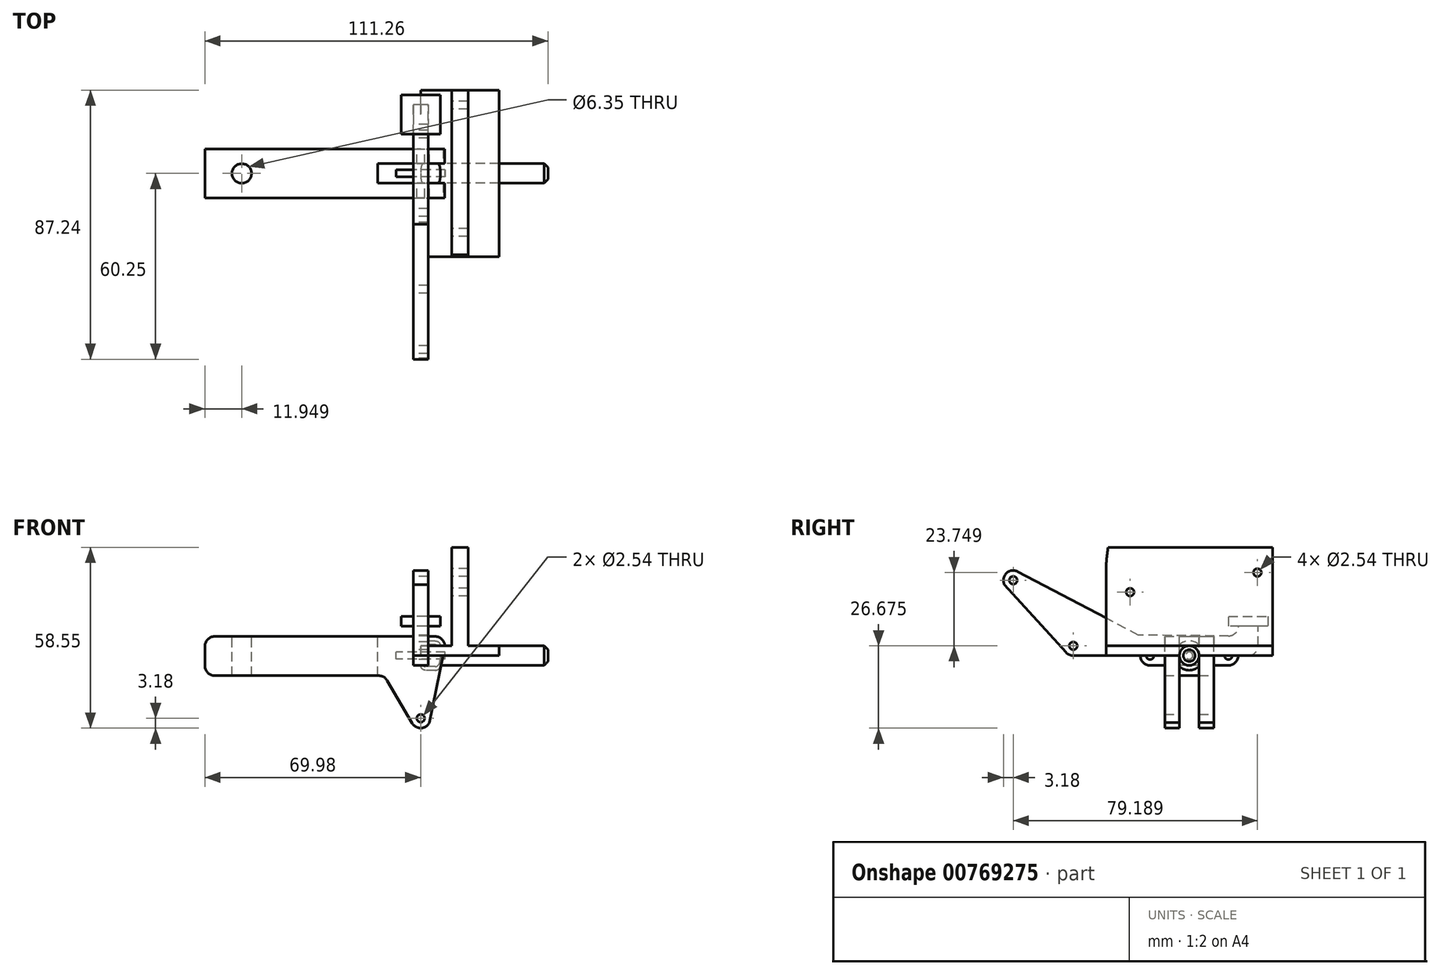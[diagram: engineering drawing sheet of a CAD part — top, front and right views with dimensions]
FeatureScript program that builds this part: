
annotation { "Feature Type Name" : "Feature", "Feature Type Description" : "" }
export const myFeature = defineFeature(function(context is Context, id is Id, definition is map)
    precondition{}
    {
        {
            var Q0;
            Q0=qCreatedBy(makeId("Front.planeOp"),FACE);
            var sketch = newSketch(context, id + "F0", { "sketchPlane" : qUnion([Q0])});
            skCircle(sketch, "E0", {"center": v(0, 0) * mm, "radius": 1.27 * mm});
            skLineSegment(sketch, "E1", {"start": v(-24.73, 6.19) * mm, "end": v(4.64, 6.19) * mm});
            skLineSegment(sketch, "E2", {"start": v(7.75, 2.38) * mm, "end": v(2.83, -21.75) * mm});
            skLineSegment(sketch, "E3", {"start": v(-2.74, -21.93) * mm, "end": v(-10.89, -8.08) * mm});
            skLineSegment(sketch, "E4", {"start": v(-13.62, -6.51) * mm, "end": v(-66.8, -6.51) * mm});
            skLineSegment(sketch, "E5", {"start": v(-69.98, -3.34) * mm, "end": v(-69.98, 3.01) * mm});
            skLineSegment(sketch, "E6", {"start": v(-66.8, 6.19) * mm, "end": v(-24.73, 6.19) * mm});
            skPoint(sketch, "E7.visualSharp", {"position": v(8.53, 6.19) * mm});
            skArc(sketch, "E7.filletArc", {"start": v(7.75, 2.38) * mm, "mid": v(7.1, 5.02) * mm, "end": v(4.64, 6.19) * mm});
            skPoint(sketch, "E8.visualSharp", {"position": v(-11.8, -6.51) * mm});
            skArc(sketch, "E8.filletArc", {"start": v(-10.89, -8.08) * mm, "mid": v(-12.05, -6.93) * mm, "end": v(-13.62, -6.51) * mm});
            skPoint(sketch, "E9.visualSharp", {"position": v(-69.98, 6.19) * mm});
            skArc(sketch, "E9.filletArc", {"start": v(-66.8, 6.19) * mm, "mid": v(-69.05, 5.26) * mm, "end": v(-69.98, 3.01) * mm});
            skPoint(sketch, "E10.visualSharp", {"position": v(-69.98, -6.51) * mm});
            skArc(sketch, "E10.filletArc", {"start": v(-69.98, -3.34) * mm, "mid": v(-69.05, -5.58) * mm, "end": v(-66.8, -6.51) * mm});
            skArc(sketch, "E11", {"start": v(-2.74, -21.93) * mm, "mid": v(0.1, -23.5) * mm, "end": v(2.83, -21.75) * mm});
            skLineSegment(sketch, "E12", {"start": v(0, 0) * mm, "end": v(-69.98, -0.16) * mm, "construction": true});
            skCircle(sketch, "E13", {"center": v(0, -20.32) * mm, "radius": 1.27 * mm});
            skLineSegment(sketch, "E14", {"start": v(0, 0) * mm, "end": v(0, -20.32) * mm, "construction": true});
            skSolve(sketch);
        }
        {
            var Q0;
            Q0=qSketchRegion(id+"F0",true);
            extrude(context, id + "F1", {"entities" : qUnion([Q0]), "endBound" : BoundingType.SYMMETRIC, "depth" : 15.88 * mm, "offsetDistance" : 25.4 * mm});
        }
        {
            var Q0;
            Q0=makeQuery(id+"F1.opExtrude","SWEPT_FACE",FACE,{"disambiguationData":[OSD([sQuery(id+"F0.wireOp",EDGE,"E1"),sQuery(id+"F0.wireOp",EDGE,"E6")])]});
            var sketch = newSketch(context, id + "F2", { "sketchPlane" : qUnion([Q0])});
            skLineSegment(sketch, "E15.0", {"start": v(7.75, -7.94) * mm, "end": v(7.75, 7.94) * mm});
            skLineSegment(sketch, "E16", {"start": v(7.75, 3.18) * mm, "end": v(-13.88, 3.18) * mm});
            skLineSegment(sketch, "E17", {"start": v(-13.88, 3.18) * mm, "end": v(-13.88, -3.17) * mm});
            skLineSegment(sketch, "E18", {"start": v(-13.88, -3.17) * mm, "end": v(7.75, -3.17) * mm});
            skLineSegment(sketch, "E19", {"start": v(7.75, 0) * mm, "end": v(-66.8, 0) * mm, "construction": true});
            skCircle(sketch, "E20", {"center": v(-58.03, 0) * mm, "radius": 3.18 * mm});
            skLineSegment(sketch, "E21.0", {"start": v(-66.8, 7.94) * mm, "end": v(4.64, 7.94) * mm});
            skLineSegment(sketch, "E22.0", {"start": v(-66.8, -7.94) * mm, "end": v(4.64, -7.94) * mm});
            skSolve(sketch);
        }
        {
            var Q0;
            Q0=qSketchRegion(id+"F2",true);
            extrude(context, id + "F3", {"entities" : qUnion([Q0]), "operationType" : NewBodyOperationType.REMOVE, "endBound" : BoundingType.THROUGH_ALL, "oppositeDirection" : true, "depth" : 25.4 * mm, "offsetDistance" : 25.4 * mm});
        }
        {
            var Q0;
            {var subQ2=sQuery(id+"F0.wireOp",EDGE,"E2");Q0=makeQuery(id+"F3.boolean.opBoolean","SPLIT",FACE,{"disambiguationData":[TD([makeQuery(id+"F3.opExtrude","SWEPT_FACE",FACE,{"disambiguationData":[OSD([sQuery(id+"F2.wireOp",EDGE,"E16")])]})])],"derivedFrom":makeQuery(id+"F1.opExtrude","SWEPT_FACE",FACE,{"disambiguationData":[OSD([subQ2])]})});}
            var sketch = newSketch(context, id + "F4", { "sketchPlane" : qUnion([Q0])});
            skLineSegment(sketch, "E23.0", {"start": v(-3.17, 3.88) * mm, "end": v(3.18, 3.88) * mm});
            skLineSegment(sketch, "E24.0", {"start": v(3.18, 5.12) * mm, "end": v(-3.17, 5.12) * mm});
            skLineSegment(sketch, "E25", {"start": v(3.18, 5.12) * mm, "end": v(3.18, 3.88) * mm});
            skLineSegment(sketch, "E26", {"start": v(-3.17, 5.12) * mm, "end": v(-3.17, 3.88) * mm});
            skSolve(sketch);
        }
        {
            var Q0;
            Q0=qSketchRegion(id+"F4",true);
            extrude(context, id + "F5", {"entities" : qUnion([Q0]), "operationType" : NewBodyOperationType.REMOVE, "oppositeDirection" : true, "depth" : 7.85 * mm, "offsetDistance" : 25.4 * mm});
        }
        {
            var Q0;
            Q0=qCreatedBy(makeId("Front.planeOp"),FACE);
            var sketch = newSketch(context, id + "F6", { "sketchPlane" : qUnion([Q0])});
            skLineSegment(sketch, "E27", {"start": v(0, 0) * mm, "end": v(25.4, 0) * mm});
            skLineSegment(sketch, "E28", {"start": v(0, 0) * mm, "end": v(0, 3.18) * mm});
            skLineSegment(sketch, "E29", {"start": v(0, 3.18) * mm, "end": v(15.36, 3.18) * mm});
            skLineSegment(sketch, "E30", {"start": v(25.4, 0) * mm, "end": v(25.4, 3.18) * mm});
            skLineSegment(sketch, "E31", {"start": v(25.4, 3.18) * mm, "end": v(10.04, 3.18) * mm});
            skLineSegment(sketch, "E32", {"start": v(15.36, 3.18) * mm, "end": v(15.36, 35.05) * mm});
            skLineSegment(sketch, "E33", {"start": v(10.04, 35.05) * mm, "end": v(15.36, 35.05) * mm});
            skLineSegment(sketch, "E34", {"start": v(10.04, 35.05) * mm, "end": v(10.04, 3.18) * mm});
            skSolve(sketch);
        }
        {
            var Q0;
            Q0=qSketchRegion(id+"F6",true);
            extrude(context, id + "F7", {"entities" : qUnion([Q0]), "endBound" : BoundingType.SYMMETRIC, "depth" : 53.97 * mm, "offsetDistance" : 25.4 * mm});
        }
        {
            var Q0;
            Q0=makeQuery(id+"F7.opExtrude","SWEPT_FACE",FACE,{"disambiguationData":[OSD([sQuery(id+"F6.wireOp",EDGE,"E34")])]});
            var sketch = newSketch(context, id + "F8", { "sketchPlane" : qUnion([Q0])});
            skLineSegment(sketch, "E35.0.0", {"start": v(-26.99, 13.43) * mm, "end": v(-26.99, 3.18) * mm});
            skLineSegment(sketch, "E35.0.2", {"start": v(26.99, 3.18) * mm, "end": v(26.99, 26.92) * mm});
            skLineSegment(sketch, "E35.0.3", {"start": v(-26.99, 3.18) * mm, "end": v(26.99, 3.18) * mm});
            skPoint(sketch, "E36.visualSharp", {"position": v(26.99, 35.05) * mm});
            skLineSegment(sketch, "E37.0.0", {"start": v(-26.99, 0) * mm, "end": v(-26.99, 3.17) * mm});
            skLineSegment(sketch, "E37.0.1", {"start": v(-26.99, 3.17) * mm, "end": v(26.99, 3.17) * mm});
            skLineSegment(sketch, "E37.0.2", {"start": v(26.99, 3.17) * mm, "end": v(26.99, 0) * mm});
            skLineSegment(sketch, "E37.0.3", {"start": v(26.99, 0) * mm, "end": v(-26.99, 0) * mm});
            skArc(sketch, "E38", {"start": v(-71.23, 26.92) * mm, "mid": v(-22.12, 76.03) * mm, "end": v(26.99, 26.92) * mm});
            skCircle(sketch, "E39", {"center": v(-22.12, 26.92) * mm, "radius": 1.27 * mm});
            skLineSegment(sketch, "E40", {"start": v(-65.76, 17.46) * mm, "end": v(-71.23, 26.92) * mm});
            skLineSegment(sketch, "E41", {"start": v(-68.51, 12.7) * mm, "end": v(9.87, 12.7) * mm});
            skPoint(sketch, "E42.visualSharp", {"position": v(-63.01, 12.7) * mm});
            skArc(sketch, "E42.filletArc", {"start": v(-65.76, 17.46) * mm, "mid": v(-71.26, 17.46) * mm, "end": v(-68.51, 12.7) * mm});
            skPoint(sketch, "E43.visualSharp", {"position": v(12.82, 12.7) * mm});
            skArc(sketch, "E43.filletArc", {"start": v(9.87, 12.7) * mm, "mid": v(12.03, 13.55) * mm, "end": v(13.04, 15.65) * mm});
            skCircle(sketch, "E44", {"center": v(19.16, 20.57) * mm, "radius": 1.27 * mm});
            skLineSegment(sketch, "E45", {"start": v(13.04, 15.65) * mm, "end": v(15.32, 26.92) * mm});
            skLineSegment(sketch, "E46", {"start": v(15.32, 26.92) * mm, "end": v(22.7, 26.67) * mm});
            skLineSegment(sketch, "E47", {"start": v(22.7, 26.67) * mm, "end": v(-26.99, 13.43) * mm});
            skPoint(sketch, "E48.orphan", {"position": v(-26.99, 35.05) * mm});
            skSolve(sketch);
        }
        {
            var Q0;
            {var subQ4=sQuery(id+"F8.wireOp",EDGE,"E38");Q0=makeQuery(id+"F8.imprint","IMPRINT",FACE,{"disambiguationData":[TD([[makeQuery(id+"F8.imprint","IMPRINT",EDGE,{"derivedFrom":subQ4}),-1.0]])]});}
            var Q1;
            Q1=makeQuery(id+"F8.imprint","IMPRINT",FACE,{"disambiguationData":[TD([[makeQuery(id+"F8.imprint","IMPRINT",EDGE,{"derivedFrom":sQuery(id+"F8.wireOp",EDGE,"E39")}),1.0]])]});
            var Q2;
            Q2=makeQuery(id+"F8.imprint","IMPRINT",FACE,{"disambiguationData":[TD([[makeQuery(id+"F8.imprint","IMPRINT",EDGE,{"derivedFrom":sQuery(id+"F8.wireOp",EDGE,"E44")}),1.0]])]});
            extrude(context, id + "F9", {"entities" : qUnion([Q0, Q1, Q2]), "operationType" : NewBodyOperationType.REMOVE, "endBound" : BoundingType.THROUGH_ALL, "oppositeDirection" : true, "depth" : 25.4 * mm, "offsetDistance" : 25.4 * mm});
        }
        {
            var Q0;
            Q0=qCreatedBy(makeId("Right.planeOp"),FACE);
            var sketch = newSketch(context, id + "F10", { "sketchPlane" : qUnion([Q0])});
            skLineSegment(sketch, "E49", {"start": v(0, 0) * mm, "end": v(19.13, 0) * mm});
            skLineSegment(sketch, "E50", {"start": v(22.3, 3.18) * mm, "end": v(22.3, 6.35) * mm});
            skLineSegment(sketch, "E51", {"start": v(12.75, 6.38) * mm, "end": v(0, 6.49) * mm});
            skLineSegment(sketch, "E52", {"start": v(27.19, 9.52) * mm, "end": v(27.19, 0) * mm, "construction": true});
            skLineSegment(sketch, "E53", {"start": v(22.3, 3.17) * mm, "end": v(0, 3.17) * mm, "construction": true});
            skLineSegment(sketch, "E54", {"start": v(15.95, 9.55) * mm, "end": v(15.95, 9.55) * mm});
            skLineSegment(sketch, "E55", {"start": v(22.3, 6.35) * mm, "end": v(22.3, 9.55) * mm});
            skLineSegment(sketch, "E56", {"start": v(22.3, 9.55) * mm, "end": v(15.95, 9.55) * mm});
            skLineSegment(sketch, "E57", {"start": v(15.95, 9.55) * mm, "end": v(12.78, 9.55) * mm});
            skLineSegment(sketch, "E58", {"start": v(12.78, 9.55) * mm, "end": v(12.78, 12.73) * mm});
            skLineSegment(sketch, "E59", {"start": v(12.78, 12.73) * mm, "end": v(25.48, 12.73) * mm});
            skLineSegment(sketch, "E60", {"start": v(25.48, 12.73) * mm, "end": v(25.48, 9.55) * mm});
            skLineSegment(sketch, "E61", {"start": v(25.48, 9.55) * mm, "end": v(22.3, 9.55) * mm});
            skPoint(sketch, "E62.visualSharp", {"position": v(22.3, 0) * mm});
            skArc(sketch, "E62.filletArc", {"start": v(19.13, 0) * mm, "mid": v(21.37, 0.93) * mm, "end": v(22.3, 3.18) * mm});
            skPoint(sketch, "E63.visualSharp", {"position": v(15.95, 6.35) * mm});
            skArc(sketch, "E63.filletArc", {"start": v(12.75, 6.38) * mm, "mid": v(15.02, 7.3) * mm, "end": v(15.95, 9.55) * mm});
            skLineSegment(sketch, "E64", {"start": v(0, 6.49) * mm, "end": v(-16.47, 6.63) * mm});
            skLineSegment(sketch, "E65", {"start": v(-16.47, 6.63) * mm, "end": v(-55.6, 27.23) * mm});
            skLineSegment(sketch, "E66", {"start": v(0, 0) * mm, "end": v(-37.6, 0) * mm});
            skLineSegment(sketch, "E67", {"start": v(-39.95, 1.04) * mm, "end": v(-59.93, 23.04) * mm});
            skArc(sketch, "E68", {"start": v(-55.6, 27.23) * mm, "mid": v(-59.27, 26.7) * mm, "end": v(-59.93, 23.04) * mm});
            skPoint(sketch, "E69.visualSharp", {"position": v(-39, 0) * mm});
            skArc(sketch, "E69.filletArc", {"start": v(-39.95, 1.04) * mm, "mid": v(-38.89, 0.27) * mm, "end": v(-37.6, 0) * mm});
            skLineSegment(sketch, "E70", {"start": v(-57.07, 24.42) * mm, "end": v(-37.6, 3.17) * mm, "construction": true});
            skLineSegment(sketch, "E71", {"start": v(-37.6, 3.17) * mm, "end": v(0, 3.17) * mm, "construction": true});
            skCircle(sketch, "E72", {"center": v(-37.6, 3.17) * mm, "radius": 1.27 * mm});
            skCircle(sketch, "E73", {"center": v(-57.07, 24.42) * mm, "radius": 1.27 * mm});
            skLineSegment(sketch, "E74", {"start": v(19.13, 9.55) * mm, "end": v(19.13, 0) * mm, "construction": true});
            skSolve(sketch);
        }
        {
            var Q0;
            Q0=makeQuery(id+"F10.imprint","IMPRINT",FACE,{"disambiguationData":[TD([[makeQuery(id+"F10.imprint","IMPRINT",EDGE,{"derivedFrom":sQuery(id+"F10.wireOp",EDGE,"E49")}),1.0]])]});
            extrude(context, id + "F11", {"entities" : qUnion([Q0]), "endBound" : BoundingType.SYMMETRIC, "depth" : 4.78 * mm, "offsetDistance" : 25.4 * mm});
        }
        {
            var Q0;
            Q0=makeQuery(id+"F10.imprint","IMPRINT",FACE,{"disambiguationData":[TD([[makeQuery(id+"F10.imprint","IMPRINT",EDGE,{"derivedFrom":sQuery(id+"F10.wireOp",EDGE,"E56")}),-1.0]])]});
            extrude(context, id + "F12", {"entities" : qUnion([Q0]), "operationType" : NewBodyOperationType.ADD, "endBound" : BoundingType.SYMMETRIC, "depth" : 12.7 * mm, "offsetDistance" : 25.4 * mm});
        }
        {
            var Q0;
            Q0=qCreatedBy(makeId("Right.planeOp"),FACE);
            var sketch = newSketch(context, id + "F13", { "sketchPlane" : qUnion([Q0])});
            skLineSegment(sketch, "E75.bottom", {"start": v(12.7, 3.17) * mm, "end": v(-12.7, 3.17) * mm});
            skLineSegment(sketch, "E75.top", {"start": v(12.7, -3.18) * mm, "end": v(-12.7, -3.18) * mm});
            skLineSegment(sketch, "E75.left", {"start": v(12.7, 3.17) * mm, "end": v(12.7, -3.18) * mm, "construction": true});
            skLineSegment(sketch, "E75.right", {"start": v(-12.7, 3.17) * mm, "end": v(-12.7, -3.18) * mm, "construction": true});
            skPoint(sketch, "E75.middle", {"position": v(0, 0) * mm});
            skArc(sketch, "E76", {"start": v(12.7, -3.18) * mm, "mid": v(15.88, 0) * mm, "end": v(12.7, 3.17) * mm});
            skArc(sketch, "E77", {"start": v(-12.7, 3.17) * mm, "mid": v(-15.88, 0) * mm, "end": v(-12.7, -3.18) * mm});
            skCircle(sketch, "E78", {"center": v(-12.7, 0) * mm, "radius": 1.27 * mm});
            skCircle(sketch, "E79", {"center": v(12.7, 0) * mm, "radius": 1.27 * mm});
            skSolve(sketch);
        }
        {
            var Q0;
            Q0=qSketchRegion(id+"F13",true);
            extrude(context, id + "F14", {"entities" : qUnion([Q0]), "endBound" : BoundingType.SYMMETRIC, "depth" : 4.78 * mm, "offsetDistance" : 25.4 * mm});
        }
        {
            var Q0;
            Q0=qCreatedBy(makeId("Right.planeOp"),FACE);
            var sketch = newSketch(context, id + "F15", { "sketchPlane" : qUnion([Q0])});
            skCircle(sketch, "E80", {"center": v(0, 0) * mm, "radius": 1.14 * mm});
            skSolve(sketch);
        }
        {
            var Q0;
            Q0=qSketchRegion(id+"F15",true);
            extrude(context, id + "F16", {"entities" : qUnion([Q0]), "endBound" : BoundingType.SYMMETRIC, "depth" : 15.88 * mm, "offsetDistance" : 25.4 * mm});
        }
        {
            var Q0;
            Q0=qCreatedBy(makeId("Right.planeOp"),FACE);
            var sketch = newSketch(context, id + "F17", { "sketchPlane" : qUnion([Q0])});
            skCircle(sketch, "E81", {"center": v(0, 0) * mm, "radius": 4.76 * mm});
            skCircle(sketch, "E82", {"center": v(0, 0) * mm, "radius": 3.18 * mm});
            skSolve(sketch);
        }
        {
            var Q0;
            Q0=makeQuery(id+"F17.imprint","IMPRINT",FACE,{"disambiguationData":[TD([[makeQuery(id+"F17.imprint","IMPRINT",EDGE,{"derivedFrom":sQuery(id+"F17.wireOp",EDGE,"E82")}),1.0]])]});
            extrude(context, id + "F18", {"entities" : qUnion([Q0]), "depth" : 41.27 * mm, "offsetDistance" : 25.4 * mm});
        }
        {
            var Q0;
            Q0=makeQuery(id+"F17.imprint","IMPRINT",FACE,{"disambiguationData":[TD([[makeQuery(id+"F17.imprint","IMPRINT",EDGE,{"derivedFrom":sQuery(id+"F17.wireOp",EDGE,"E81")}),1.0]])]});
            extrude(context, id + "F19", {"entities" : qUnion([Q0]), "operationType" : NewBodyOperationType.ADD, "depth" : 6.35 * mm, "offsetDistance" : 25.4 * mm});
        }
        {
            var Q0;
            Q0=makeQuery(id+"F19.opExtrude","CAP_EDGE",EDGE,{"disambiguationData":[OSD([sQuery(id+"F17.wireOp",EDGE,"E81")])],"isStart":false});
            var Q1;
            Q1=makeQuery(id+"F19.opExtrude","CAP_EDGE",EDGE,{"disambiguationData":[OSD([sQuery(id+"F17.wireOp",EDGE,"E81")])],"isStart":true});
            fillet(context, id + "F20", {"entities" : qUnion([Q0, Q1]), "radius" : 1.59 * mm, "tangentPropagation" : true, "allowEdgeOverflow" : false});
        }
        {
            var Q0;
            Q0=makeQuery(id+"F18.opExtrude","CAP_EDGE",EDGE,{"disambiguationData":[OSD([sQuery(id+"F17.wireOp",EDGE,"E82")])],"isStart":false});
            chamfer(context, id + "F21", {"entities" : qUnion([Q0]), "width" : 1.27 * mm, "tangentPropagation" : true});
        }
    });
